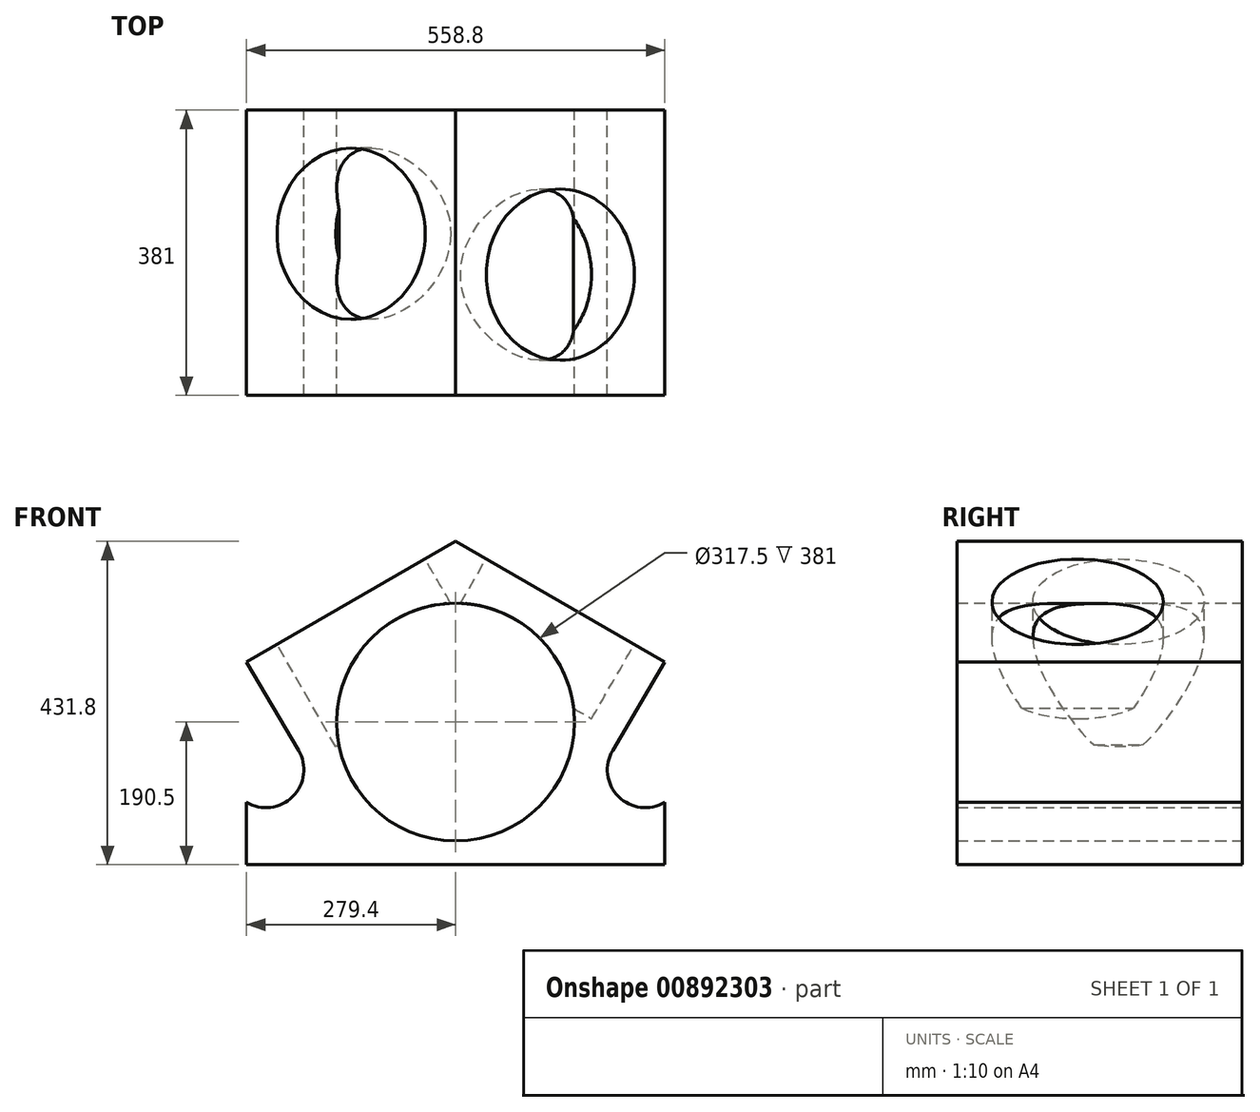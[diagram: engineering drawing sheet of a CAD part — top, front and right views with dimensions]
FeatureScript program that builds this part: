
annotation { "Feature Type Name" : "Feature", "Feature Type Description" : "" }
export const myFeature = defineFeature(function(context is Context, id is Id, definition is map)
    precondition{}
    {
        {
            var Q0;
            Q0=qCreatedBy(makeId("Front.planeOp"),FACE);
            var sketch = newSketch(context, id + "F0", { "sketchPlane" : qUnion([Q0])});
            skLineSegment(sketch, "E0.bottom", {"start": v(279.4, -215.9) * mm, "end": v(-279.4, -215.9) * mm});
            skLineSegment(sketch, "E0.top", {"start": v(279.4, 215.9) * mm, "end": v(-279.4, 215.9) * mm});
            skLineSegment(sketch, "E0.left", {"start": v(279.4, -215.9) * mm, "end": v(279.4, 215.9) * mm});
            skLineSegment(sketch, "E0.right", {"start": v(-279.4, -215.9) * mm, "end": v(-279.4, 215.9) * mm});
            skPoint(sketch, "E0.middle", {"position": v(0, 0) * mm});
            skLineSegment(sketch, "E1", {"start": v(0, 0) * mm, "end": v(0, 215.9) * mm});
            skLineSegment(sketch, "E2", {"start": v(0, 0) * mm, "end": v(0, -215.9) * mm});
            skLineSegment(sketch, "E3", {"start": v(0, 215.9) * mm, "end": v(-279.4, 54.68) * mm});
            skLineSegment(sketch, "E4", {"start": v(0, 215.9) * mm, "end": v(279.4, 54.68) * mm});
            skLineSegment(sketch, "E5", {"start": v(0, -25.4) * mm, "end": v(0, -215.9) * mm});
            skCircle(sketch, "E6", {"center": v(0, -25.4) * mm, "radius": 158.75 * mm});
            skLineSegment(sketch, "E7", {"start": v(279.4, -182.11) * mm, "end": v(254, -182.11) * mm});
            skCircle(sketch, "E8", {"center": v(253.5, -88.9) * mm, "radius": 50.8 * mm});
            skCircle(sketch, "E9.MirrorC", {"center": v(-253.5, -88.9) * mm, "radius": 50.8 * mm});
            skLineSegment(sketch, "E10.MirrorCS", {"start": v(-253.5, -88.9) * mm, "end": v(-253.5, -215.9) * mm});
            skLineSegment(sketch, "E11", {"start": v(-279.4, 54.68) * mm, "end": v(-209.78, -63.04) * mm});
            skLineSegment(sketch, "E12", {"start": v(279.4, 54.68) * mm, "end": v(209.78, -63.04) * mm});
            skSolve(sketch);
        }
        {
            var Q0;
            {var subQ0=sQuery(id+"F0.wireOp",EDGE,"E3");Q0=makeQuery(id+"F0.imprint","IMPRINT",FACE,{"disambiguationData":[TD([[makeQuery(id+"F0.imprint","IMPRINT",EDGE,{"derivedFrom":subQ0}),1.0]])]});}
            var Q1;
            {var subQ0=sQuery(id+"F0.wireOp",EDGE,"E0.right");var subQ1=sQuery(id+"F0.wireOp",EDGE,"E0.bottom");var subQ2=makeQuery(id+"F0.imprint","INTERSECT",VERTEX,{"derivedFrom":[subQ1,subQ0]});Q1=makeQuery(id+"F0.imprint","IMPRINT",FACE,{"disambiguationData":[TD([[makeQuery(id+"F0.imprint","IMPRINT",EDGE,{"disambiguationData":[TD([[subQ2,1.0]])],"derivedFrom":subQ1}),-1.0]])]});}
            var Q2;
            {var subQ4=sQuery(id+"F0.wireOp",EDGE,"E4");Q2=makeQuery(id+"F0.imprint","IMPRINT",FACE,{"disambiguationData":[TD([[makeQuery(id+"F0.imprint","IMPRINT",EDGE,{"derivedFrom":subQ4}),-1.0]])]});}
            extrude(context, id + "F1", {"entities" : qUnion([Q0, Q1, Q2]), "depth" : 381 * mm, "offsetDistance" : 25.4 * mm});
        }
        {
            var Q0;
            Q0=makeQuery(id+"F1.opExtrude","SWEPT_FACE",FACE,{"disambiguationData":[OSD([sQuery(id+"F0.wireOp",EDGE,"E4")])]});
            var sketch = newSketch(context, id + "F2", { "sketchPlane" : qUnion([Q0])});
            skCircle(sketch, "E13", {"center": v(53.38, -219.71) * mm, "radius": 114.3 * mm});
            skPoint(sketch, "E14", {"position": v(-60.92, -105.41) * mm});
            skPoint(sketch, "E15", {"position": v(167.68, -105.41) * mm});
            skPoint(sketch, "E16", {"position": v(167.68, -334.01) * mm});
            skPoint(sketch, "E17", {"position": v(-60.92, -334.01) * mm});
            skSolve(sketch);
        }
        {
            var Q0;
            Q0=makeQuery(id+"F2.imprint","IMPRINT",FACE,{"disambiguationData":[TD([[makeQuery(id+"F2.imprint","IMPRINT",EDGE,{"derivedFrom":sQuery(id+"F2.wireOp",EDGE,"E13")}),1.0]])]});
            extrude(context, id + "F3", {"entities" : qUnion([Q0]), "operationType" : NewBodyOperationType.REMOVE, "oppositeDirection" : true, "depth" : 114.3 * mm, "offsetDistance" : 25.4 * mm});
        }
        {
            var Q0;
            Q0=makeQuery(id+"F1.opExtrude","SWEPT_FACE",FACE,{"disambiguationData":[OSD([sQuery(id+"F0.wireOp",EDGE,"E3")])]});
            var sketch = newSketch(context, id + "F4", { "sketchPlane" : qUnion([Q0])});
            skCircle(sketch, "E18", {"center": v(-53.38, -165.1) * mm, "radius": 114.3 * mm});
            skPoint(sketch, "E19", {"position": v(-167.68, -50.8) * mm});
            skPoint(sketch, "E20", {"position": v(60.92, -50.8) * mm});
            skPoint(sketch, "E21", {"position": v(60.92, -279.4) * mm});
            skPoint(sketch, "E22", {"position": v(-167.68, -279.4) * mm});
            skSolve(sketch);
        }
        {
            var Q0;
            Q0 = qSketchRegion(id + "F4", true);
            extrude(context, id + "F5", {"entities" : qUnion([Q0]), "operationType" : NewBodyOperationType.REMOVE, "oppositeDirection" : true, "depth" : 157.48 * mm, "offsetDistance" : 25.4 * mm});
        }
    });
